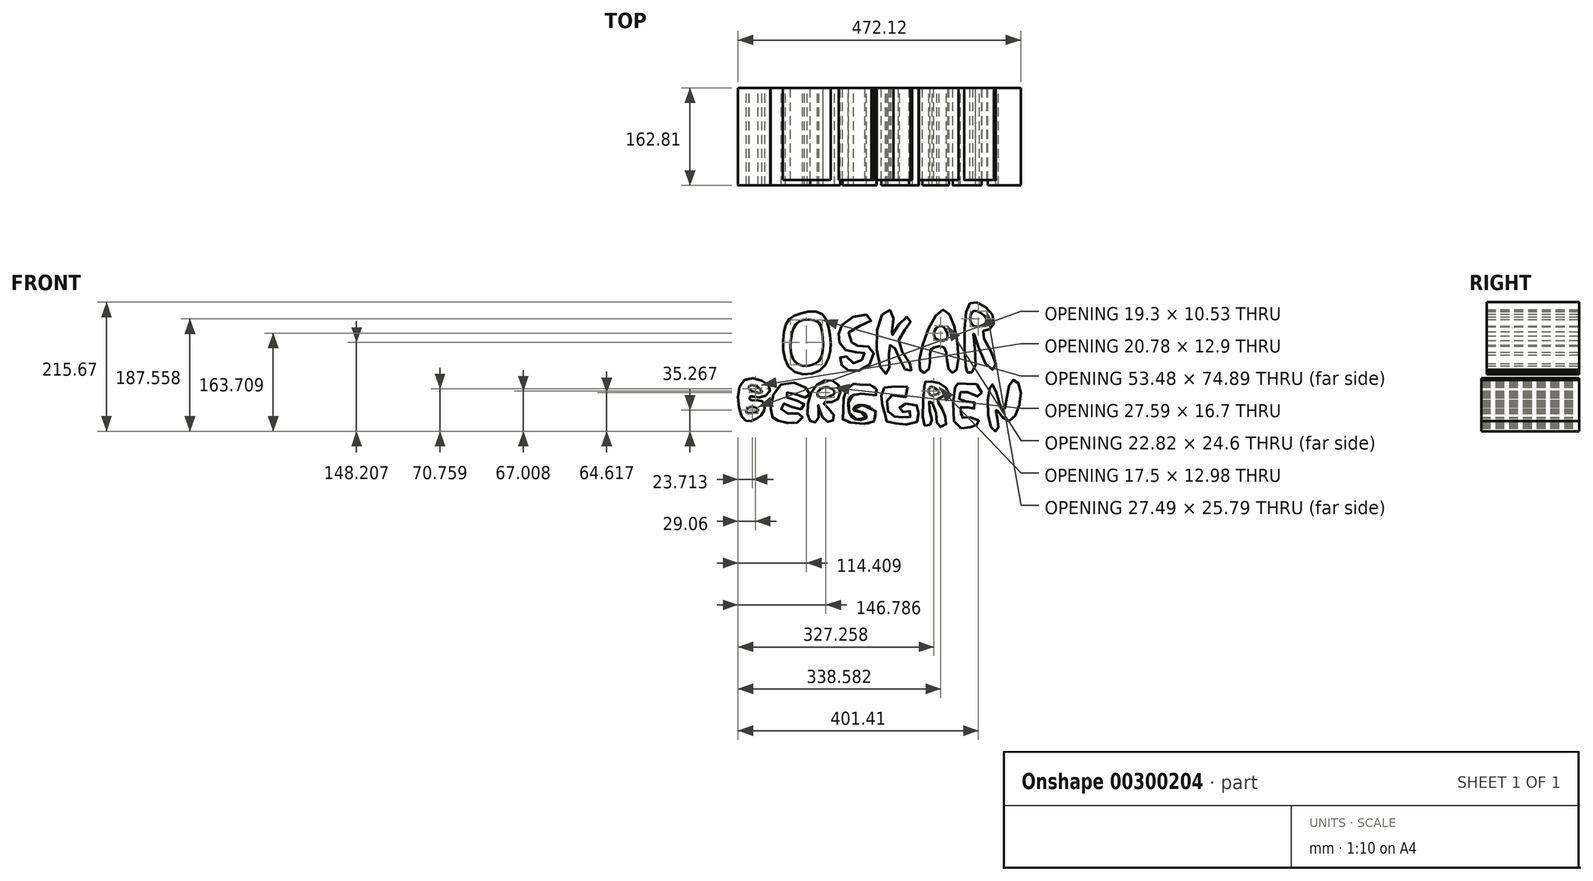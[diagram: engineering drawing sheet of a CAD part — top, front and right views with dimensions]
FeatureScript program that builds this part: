
annotation { "Feature Type Name" : "Feature", "Feature Type Description" : "" }
export const myFeature = defineFeature(function(context is Context, id is Id, definition is map)
    precondition{}
    {
        {
            var Q0;
            Q0=qCreatedBy(makeId("Front.planeOp"),FACE);
            var sketch = newSketch(context, id + "F0", { "sketchPlane" : qUnion([Q0])});
            skFitSpline(sketch, "E0", {"points": [v(-126, 54.05) * mm, v(-147.35, 41.31) * mm, v(-155.27, 3.79) * mm, v(-140.46, -40.97) * mm, v(-97.09, -43.38) * mm, v(-77.46, -14.8) * mm, v(-77.8, 24.79) * mm, v(-91.58, 54.05) * mm, v(-126, 54.05) * mm]});
            skFitSpline(sketch, "E1", {"points": [v(-121.18, 42.69) * mm, v(-134.62, 34.77) * mm, v(-142.54, 5.85) * mm, v(-133.59, -28.92) * mm, v(-105, -31.67) * mm, v(-89.84, -15.5) * mm, v(-89.84, 21.34) * mm, v(-97.07, 39.94) * mm, v(-121.18, 42.69) * mm]});
            skFitSpline(sketch, "E2", {"points": [v(-16.12, 51.99) * mm, v(-8.54, 40.97) * mm, v(-44.02, 24.44) * mm, v(-39.89, 4.48) * mm, v(-29.2, 0) * mm, v(-6.81, -4.48) * mm, v(-8.54, -28.23) * mm, v(-36.79, -42.69) * mm, v(-53.32, -36.84) * mm, v(-60.9, -23.07) * mm, v(-53.32, -15.5) * mm, v(-37.82, -29.26) * mm, v(-21.63, -21.34) * mm, v(-19.56, -12.05) * mm, v(-39.2, -11.02) * mm, v(-58.49, 0) * mm, v(-62.28, 18.94) * mm, v(-54.35, 36.84) * mm, v(-16.12, 51.99) * mm]});
            skFitSpline(sketch, "E3", {"points": [v(10.06, 51.99) * mm, v(10.4, -42.35) * mm, v(21.09, -44.41) * mm, v(22.47, 0) * mm, v(32.11, -5.16) * mm, v(51.06, -41.66) * mm, v(60.36, -38.21) * mm, v(37.62, 5.85) * mm, v(57.95, 40.28) * mm, v(49.34, 47.17) * mm, v(25.91, 16.53) * mm, v(27.98, 55.08) * mm, v(10.06, 51.99) * mm]});
            skFitSpline(sketch, "E4", {"points": [v(73.45, -40.97) * mm, v(87.57, -40.62) * mm, v(90.33, -9.3) * mm, v(97.9, -3.1) * mm, v(114.44, -3.44) * mm, v(122.02, -40.62) * mm, v(134.08, -41.31) * mm, v(113.41, 59.9) * mm, v(73.45, -40.97) * mm]});
            skFitSpline(sketch, "E5", {"points": [v(108.24, 33.05) * mm, v(97.56, 14.46) * mm, v(118.58, 12.05) * mm, v(108.24, 33.05) * mm]});
            skFitSpline(sketch, "E6", {"points": [v(150.27, 56.46) * mm, v(152, -43.72) * mm, v(153.72, -44.41) * mm, v(164.4, -40.97) * mm, v(162.33, 23.07) * mm, v(189.54, -38.56) * mm, v(200.22, -32.36) * mm, v(177.49, 22.38) * mm, v(192.3, 28.57) * mm, v(194.02, 51.99) * mm, v(165.08, 72.64) * mm, v(150.27, 56.46) * mm]});
            skFitSpline(sketch, "E7", {"points": [v(162.33, 57.5) * mm, v(160.26, 35.12) * mm, v(180.24, 34.77) * mm, v(184.37, 44.76) * mm, v(162.33, 57.5) * mm]});
            skSolve(sketch);
        }
        {
            var Q0;
            Q0=makeQuery(id+"F0.imprint","IMPRINT",FACE,{"disambiguationData":[TD([[makeQuery(id+"F0.imprint","IMPRINT",EDGE,{"derivedFrom":sQuery(id+"F0.wireOp",EDGE,"E0")}),1.0]])]});
            var Q1;
            Q1=makeQuery(id+"F0.imprint","IMPRINT",FACE,{"disambiguationData":[TD([[makeQuery(id+"F0.imprint","IMPRINT",EDGE,{"derivedFrom":sQuery(id+"F0.wireOp",EDGE,"E2")}),-1.0]])]});
            var Q2;
            Q2=makeQuery(id+"F0.imprint","IMPRINT",FACE,{"disambiguationData":[TD([[makeQuery(id+"F0.imprint","IMPRINT",EDGE,{"derivedFrom":sQuery(id+"F0.wireOp",EDGE,"E3")}),1.0]])]});
            var Q3;
            Q3=makeQuery(id+"F0.imprint","IMPRINT",FACE,{"disambiguationData":[TD([[makeQuery(id+"F0.imprint","IMPRINT",EDGE,{"derivedFrom":sQuery(id+"F0.wireOp",EDGE,"E4")}),1.0]])]});
            var Q4;
            Q4=makeQuery(id+"F0.imprint","IMPRINT",FACE,{"disambiguationData":[TD([[makeQuery(id+"F0.imprint","IMPRINT",EDGE,{"derivedFrom":sQuery(id+"F0.wireOp",EDGE,"E6")}),1.0]])]});
            extrude(context, id + "F1", {"entities" : qUnion([Q0, Q1, Q2, Q3, Q4]), "depth" : 154.18 * mm});
        }
        {
            var Q0;
            Q0=qCreatedBy(makeId("Front.planeOp"),FACE);
            var sketch = newSketch(context, id + "F2", { "sketchPlane" : qUnion([Q0])});
            skFitSpline(sketch, "E8", {"points": [v(-219.53, -57.27) * mm, v(-222.7, -120.37) * mm, v(-205.2, -124.61) * mm, v(-186.12, -107.64) * mm, v(-191.42, -91.73) * mm, v(-210.51, -90.67) * mm, v(-209.45, -84.31) * mm, v(-196.72, -86.96) * mm, v(-176.58, -71.58) * mm, v(-219.53, -57.27) * mm]});
            skFitSpline(sketch, "E9", {"points": [v(-206.8, -65.75) * mm, v(-211.57, -72.65) * mm, v(-190.9, -77.42) * mm, v(-206.8, -65.75) * mm]});
            skFitSpline(sketch, "E10", {"points": [v(-212.1, -102.87) * mm, v(-215.28, -111.88) * mm, v(-196.72, -107.64) * mm, v(-212.1, -102.87) * mm]});
            skFitSpline(sketch, "E11", {"points": [v(-158.55, -64.7) * mm, v(-174.45, -116.13) * mm, v(-161.73, -125.67) * mm, v(-128.85, -127.26) * mm, v(-124.08, -115.07) * mm, v(-154.83, -110.82) * mm, v(-154.83, -97.04) * mm, v(-127.26, -106.58) * mm, v(-120.37, -97.04) * mm, v(-149.53, -85.37) * mm, v(-147.41, -77.95) * mm, v(-115.6, -86.96) * mm, v(-111.35, -76.36) * mm, v(-158.55, -64.7) * mm]});
            skFitSpline(sketch, "E12", {"points": [v(-98.55, -64.7) * mm, v(-111.35, -124.08) * mm, v(-97.49, -124.61) * mm, v(-96.43, -99.16) * mm, v(-83.7, -126.2) * mm, v(-69.38, -119.3) * mm, v(-87.94, -94.92) * mm, v(-67.26, -92.26) * mm, v(-63.55, -64.7) * mm, v(-98.55, -64.7) * mm]});
            skFitSpline(sketch, "E13", {"points": [v(-87.94, -70) * mm, v(-97.49, -83.25) * mm, v(-78.93, -85.37) * mm, v(-69.38, -76.36) * mm, v(-87.94, -70) * mm]});
            skFitSpline(sketch, "E14", {"points": [v(-22.18, -65.75) * mm, v(-37.56, -63.63) * mm, v(-49.23, -72.65) * mm, v(-54, -89.61) * mm, v(-55.06, -114) * mm, v(-54, -125.67) * mm, v(-29.08, -129.38) * mm, v(-5.75, -128.32) * mm, v(0, -110.3) * mm, v(-31.73, -100.22) * mm, v(-37.03, -107.64) * mm, v(-19.53, -112.94) * mm, v(-16.88, -120.9) * mm, v(-36.5, -121.96) * mm, v(-45.52, -106.58) * mm, v(-43.93, -86.96) * mm, v(-34.38, -81.13) * mm, v(-21.12, -80.6) * mm, v(-10.52, -81.66) * mm, v(0, -82.72) * mm, v(0, -77.42) * mm, v(0, -70.52) * mm, v(-14.23, -64.7) * mm, v(-22.18, -65.75) * mm]});
            skFitSpline(sketch, "E15", {"points": [v(52.59, -68.93) * mm, v(53.12, -84.31) * mm, v(33.5, -83.25) * mm, v(20.77, -84.31) * mm, v(18.12, -91.73) * mm, v(20.24, -106.58) * mm, v(20.77, -112.94) * mm, v(28.72, -117.72) * mm, v(36.68, -119.3) * mm, v(44.63, -119.84) * mm, v(49.4, -120.37) * mm, v(57.36, -118.78) * mm, v(61.07, -111.35) * mm, v(55.77, -109.23) * mm, v(49.4, -109.23) * mm, v(45.16, -110.82) * mm, v(42.51, -110.82) * mm, v(39.33, -106.05) * mm, v(40.39, -100.75) * mm, v(47.28, -97.57) * mm, v(60.54, -97.04) * mm, v(70.09, -101.8) * mm, v(71.15, -109.23) * mm, v(71.68, -117.72) * mm, v(69.03, -126.73) * mm, v(59.48, -131.5) * mm, v(40.39, -130.97) * mm, v(31.9, -129.38) * mm, v(22.36, -127.8) * mm, v(16, -124.61) * mm, v(16, -116.13) * mm, v(13.88, -112.41) * mm, v(11.22, -102.87) * mm, v(10.16, -91.73) * mm, v(9.1, -80.07) * mm, v(12.28, -72.11) * mm, v(18.12, -68.4) * mm, v(36.15, -67.87) * mm, v(52.59, -68.93) * mm]});
            skFitSpline(sketch, "E16", {"points": [v(80.7, -68.4) * mm, v(79.63, -130.97) * mm, v(86.53, -133.62) * mm, v(93.42, -128.85) * mm, v(88.65, -102.87) * mm, v(90.77, -91.73) * mm, v(100.84, -115.6) * mm, v(104.56, -134.68) * mm, v(116.22, -132.56) * mm, v(114.1, -114) * mm, v(106.68, -99.16) * mm, v(101.9, -90.67) * mm, v(111.45, -84.31) * mm, v(121.52, -79.54) * mm, v(113.04, -66.81) * mm, v(95, -59.92) * mm, v(82.28, -60.45) * mm, v(80.7, -68.4) * mm]});
            skFitSpline(sketch, "E17", {"points": [v(90.24, -69.46) * mm, v(89.7, -81.13) * mm, v(100.31, -81.66) * mm, v(105.62, -79) * mm, v(100.84, -72.65) * mm, v(90.24, -69.46) * mm]});
            skFitSpline(sketch, "E18", {"points": [v(132.13, -69.46) * mm, v(133.2, -133.1) * mm, v(153.34, -136.8) * mm, v(165, -134.15) * mm, v(172.96, -127.8) * mm, v(161.3, -120.37) * mm, v(145.39, -120.37) * mm, v(143.27, -120.37) * mm, v(141.68, -109.23) * mm, v(141.68, -102.34) * mm, v(157.58, -104.46) * mm, v(164.48, -104.46) * mm, v(165, -95.45) * mm, v(146.45, -92.8) * mm, v(139.02, -88.55) * mm, v(141.68, -77.42) * mm, v(156, -79) * mm, v(175.08, -84.31) * mm, v(171.37, -66.81) * mm, v(148.04, -63.63) * mm, v(134.78, -63.63) * mm, v(132.13, -69.46) * mm]});
            skFitSpline(sketch, "E19", {"points": [v(191.52, -135.75) * mm, v(194.17, -64.7) * mm, v(212.2, -110.3) * mm, v(226, -59.39) * mm, v(240.84, -71.05) * mm, v(220.69, -125.67) * mm, v(200.54, -106.05) * mm, v(203.72, -139.99) * mm, v(191.52, -135.75) * mm]});
            skSolve(sketch);
        }
        {
            var Q0;
            Q0=makeQuery(id+"F2.imprint","IMPRINT",FACE,{"disambiguationData":[TD([[makeQuery(id+"F2.imprint","IMPRINT",EDGE,{"derivedFrom":sQuery(id+"F2.wireOp",EDGE,"E8")}),1.0]])]});
            var Q1;
            Q1=makeQuery(id+"F2.imprint","IMPRINT",FACE,{"disambiguationData":[TD([[makeQuery(id+"F2.imprint","IMPRINT",EDGE,{"derivedFrom":sQuery(id+"F2.wireOp",EDGE,"E11")}),1.0]])]});
            var Q2;
            Q2=makeQuery(id+"F2.imprint","IMPRINT",FACE,{"disambiguationData":[TD([[makeQuery(id+"F2.imprint","IMPRINT",EDGE,{"derivedFrom":sQuery(id+"F2.wireOp",EDGE,"E12")}),1.0]])]});
            var Q3;
            Q3=makeQuery(id+"F2.imprint","IMPRINT",FACE,{"disambiguationData":[TD([[makeQuery(id+"F2.imprint","IMPRINT",EDGE,{"derivedFrom":sQuery(id+"F2.wireOp",EDGE,"E14")}),1.0]])]});
            var Q4;
            Q4=makeQuery(id+"F2.imprint","IMPRINT",FACE,{"disambiguationData":[TD([[makeQuery(id+"F2.imprint","IMPRINT",EDGE,{"derivedFrom":sQuery(id+"F2.wireOp",EDGE,"E15")}),-1.0]])]});
            var Q5;
            Q5=makeQuery(id+"F2.imprint","IMPRINT",FACE,{"disambiguationData":[TD([[makeQuery(id+"F2.imprint","IMPRINT",EDGE,{"derivedFrom":sQuery(id+"F2.wireOp",EDGE,"E16")}),1.0]])]});
            var Q6;
            Q6=makeQuery(id+"F2.imprint","IMPRINT",FACE,{"disambiguationData":[TD([[makeQuery(id+"F2.imprint","IMPRINT",EDGE,{"derivedFrom":sQuery(id+"F2.wireOp",EDGE,"E18")}),1.0]])]});
            var Q7;
            Q7=makeQuery(id+"F2.imprint","IMPRINT",FACE,{"disambiguationData":[TD([[makeQuery(id+"F2.imprint","IMPRINT",EDGE,{"derivedFrom":sQuery(id+"F2.wireOp",EDGE,"E19")}),-1.0]])]});
            extrude(context, id + "F3", {"entities" : qUnion([Q0, Q1, Q2, Q3, Q4, Q5, Q6, Q7]), "depth" : 162.8 * mm});
        }
    });
